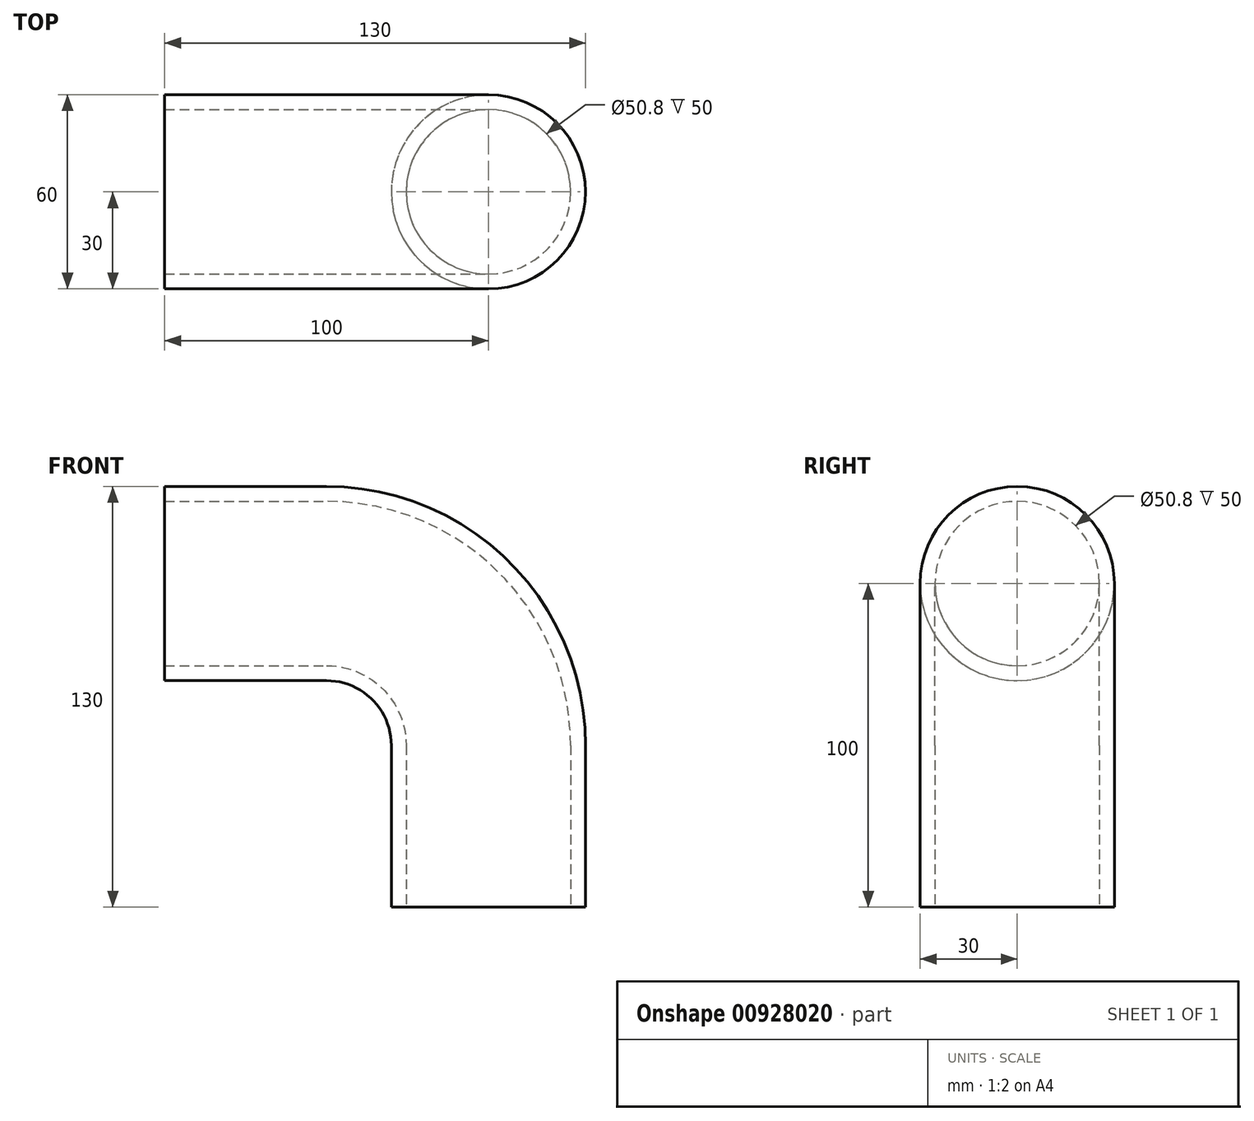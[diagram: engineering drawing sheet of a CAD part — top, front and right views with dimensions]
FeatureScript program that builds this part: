
annotation { "Feature Type Name" : "Feature", "Feature Type Description" : "" }
export const myFeature = defineFeature(function(context is Context, id is Id, definition is map)
    precondition{}
    {
        {
            var Q0;
            Q0=qCreatedBy(makeId("Right.planeOp"),FACE);
            var sketch = newSketch(context, id + "F0", { "sketchPlane" : qUnion([Q0])});
            skCircle(sketch, "E0", {"center": v(0, 0) * mm, "radius": 25.4 * mm});
            skCircle(sketch, "E1", {"center": v(0, 0) * mm, "radius": 30 * mm});
            skSolve(sketch);
        }
        {
            var Q0;
            Q0=qCreatedBy(makeId("Front.planeOp"),FACE);
            var sketch = newSketch(context, id + "F1", { "sketchPlane" : qUnion([Q0])});
            skLineSegment(sketch, "E2", {"start": v(0, 0) * mm, "end": v(50, 0) * mm});
            skLineSegment(sketch, "E3", {"start": v(100, -50) * mm, "end": v(100, -100) * mm});
            skPoint(sketch, "E4.visualSharp", {"position": v(100, 0) * mm});
            skArc(sketch, "E4.filletArc", {"start": v(100, -50) * mm, "mid": v(85.36, -14.64) * mm, "end": v(50, 0) * mm});
            skSolve(sketch);
        }
        {
            var Q0;
            Q0=makeQuery(id+"F0.imprint","IMPRINT",FACE,{"disambiguationData":[TD([[makeQuery(id+"F0.imprint","IMPRINT",EDGE,{"derivedFrom":sQuery(id+"F0.wireOp",EDGE,"E0")}),-1.0]])]});
            var Q1;
            Q1=sQuery(id+"F1.wireOp",EDGE,"E2");
            var Q2;
            Q2=sQuery(id+"F1.wireOp",EDGE,"E4.filletArc");
            var Q3;
            Q3=sQuery(id+"F1.wireOp",EDGE,"E3");
            sweep(context, id + "F2", {"profiles" : qUnion([Q0]), "path" : qUnion([Q1, Q2, Q3])});
        }
    });
